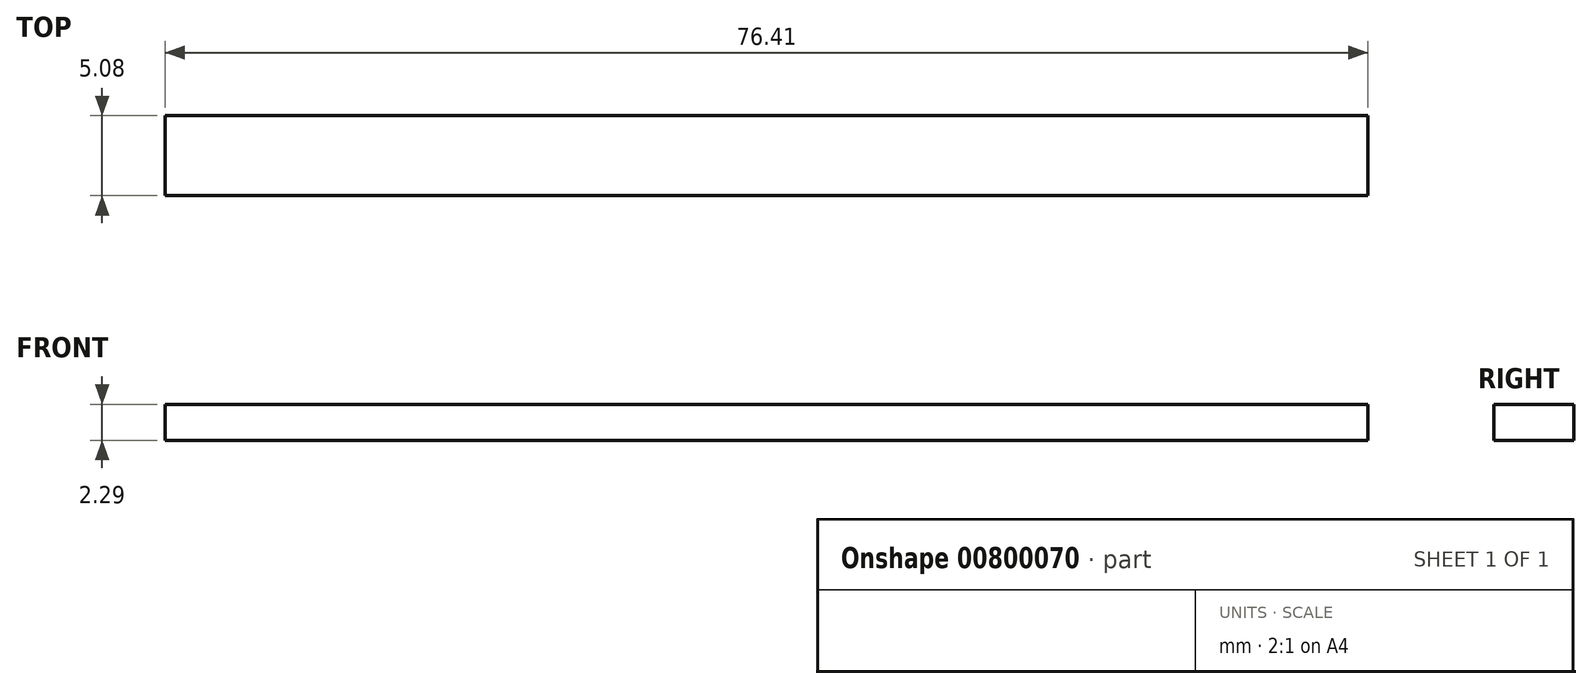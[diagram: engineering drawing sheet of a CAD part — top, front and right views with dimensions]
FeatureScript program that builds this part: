
annotation { "Feature Type Name" : "Feature", "Feature Type Description" : "" }
export const myFeature = defineFeature(function(context is Context, id is Id, definition is map)
    precondition{}
    {
        {
            var Q0;
            Q0=qCreatedBy(makeId("Top.planeOp"),FACE);
            var sketch = newSketch(context, id + "F0", { "sketchPlane" : qUnion([Q0])});
            skLineSegment(sketch, "E0.bottom", {"start": v(-76.41, 0) * mm, "end": v(0, 0) * mm});
            skLineSegment(sketch, "E0.top", {"start": v(-76.41, -5.08) * mm, "end": v(0, -5.08) * mm});
            skLineSegment(sketch, "E0.left", {"start": v(-76.41, 0) * mm, "end": v(-76.41, -5.08) * mm});
            skLineSegment(sketch, "E0.right", {"start": v(0, 0) * mm, "end": v(0, -5.08) * mm});
            skSolve(sketch);
        }
        {
            var Q0;
            Q0 = qSketchRegion(id + "F0", true);
            extrude(context, id + "F1", {"entities" : qUnion([Q0]), "oppositeDirection" : true, "depth" : 2.3 * mm, "offsetDistance" : 25.4 * mm});
        }
    });
